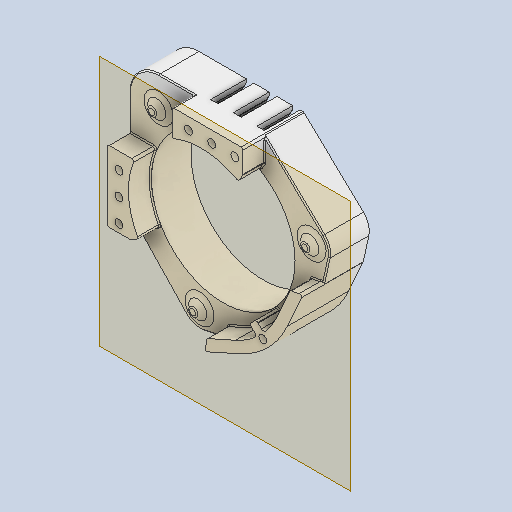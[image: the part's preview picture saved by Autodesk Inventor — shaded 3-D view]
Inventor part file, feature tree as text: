
AUTODESK INVENTOR PART (.ipt)
format: ipt  version: 2022 (Build 260153000, 153)  size: 528,384 bytes
history: native  units: in
note: dims shown in document units (in); Inventor stores cm internally (conversion verified against a paired STEP export)
features: sketch x5, other x3, plane x2
ambient origin geometry x8: Origin, YZ Plane, XZ Plane, XY Plane, X Axis, Y Axis, Z Axis, Center Point
bodies: Solid1 (feature_tree)
feature tree (10):
  other  "upper.ipt"
  other  "Solid1::upper.ipt"
  other  "TaggingFeature1"
  sketch  "Sketch1"  dims[d0=0.3937in]
  sketch  "Sketch2"
  sketch  "Sketch3"
  sketch  "Sketch5"
  sketch  "Sketch6"
  plane  "Work Plane1"
  plane  "Work Plane2"
